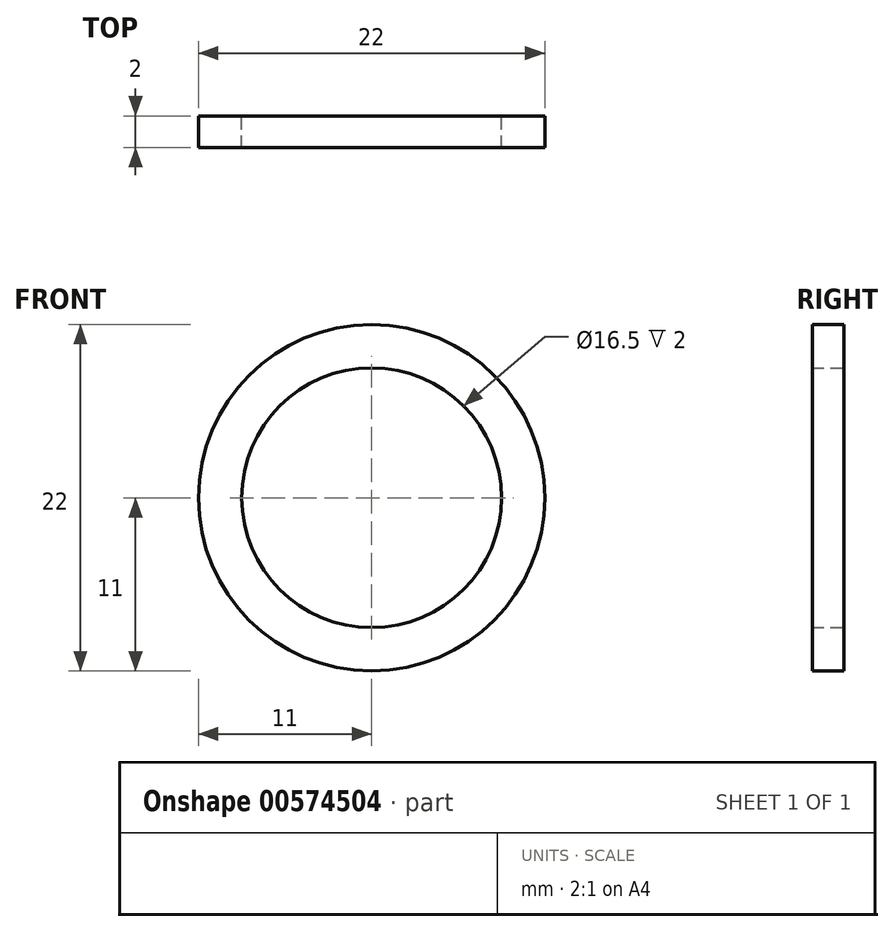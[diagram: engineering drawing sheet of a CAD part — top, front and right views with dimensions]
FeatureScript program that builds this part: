
annotation { "Feature Type Name" : "Feature", "Feature Type Description" : "" }
export const myFeature = defineFeature(function(context is Context, id is Id, definition is map)
    precondition{}
    {
        {
            var Q0;
            Q0=qCreatedBy(makeId("Front.planeOp"),FACE);
            var sketch = newSketch(context, id + "F0", { "sketchPlane" : qUnion([Q0])});
            skCircle(sketch, "E0", {"center": v(0, 0) * mm, "radius": 11 * mm});
            skCircle(sketch, "E1", {"center": v(0, 0) * mm, "radius": 8.25 * mm});
            skSolve(sketch);
        }
        {
            var Q0;
            Q0=makeQuery(id+"F0.imprint","IMPRINT",FACE,{"disambiguationData":[TD([[makeQuery(id+"F0.imprint","IMPRINT",EDGE,{"derivedFrom":sQuery(id+"F0.wireOp",EDGE,"E0")}),1.0]])]});
            extrude(context, id + "F1", {"entities" : qUnion([Q0]), "depth" : 2 * mm, "offsetDistance" : 25 * mm});
        }
    });
